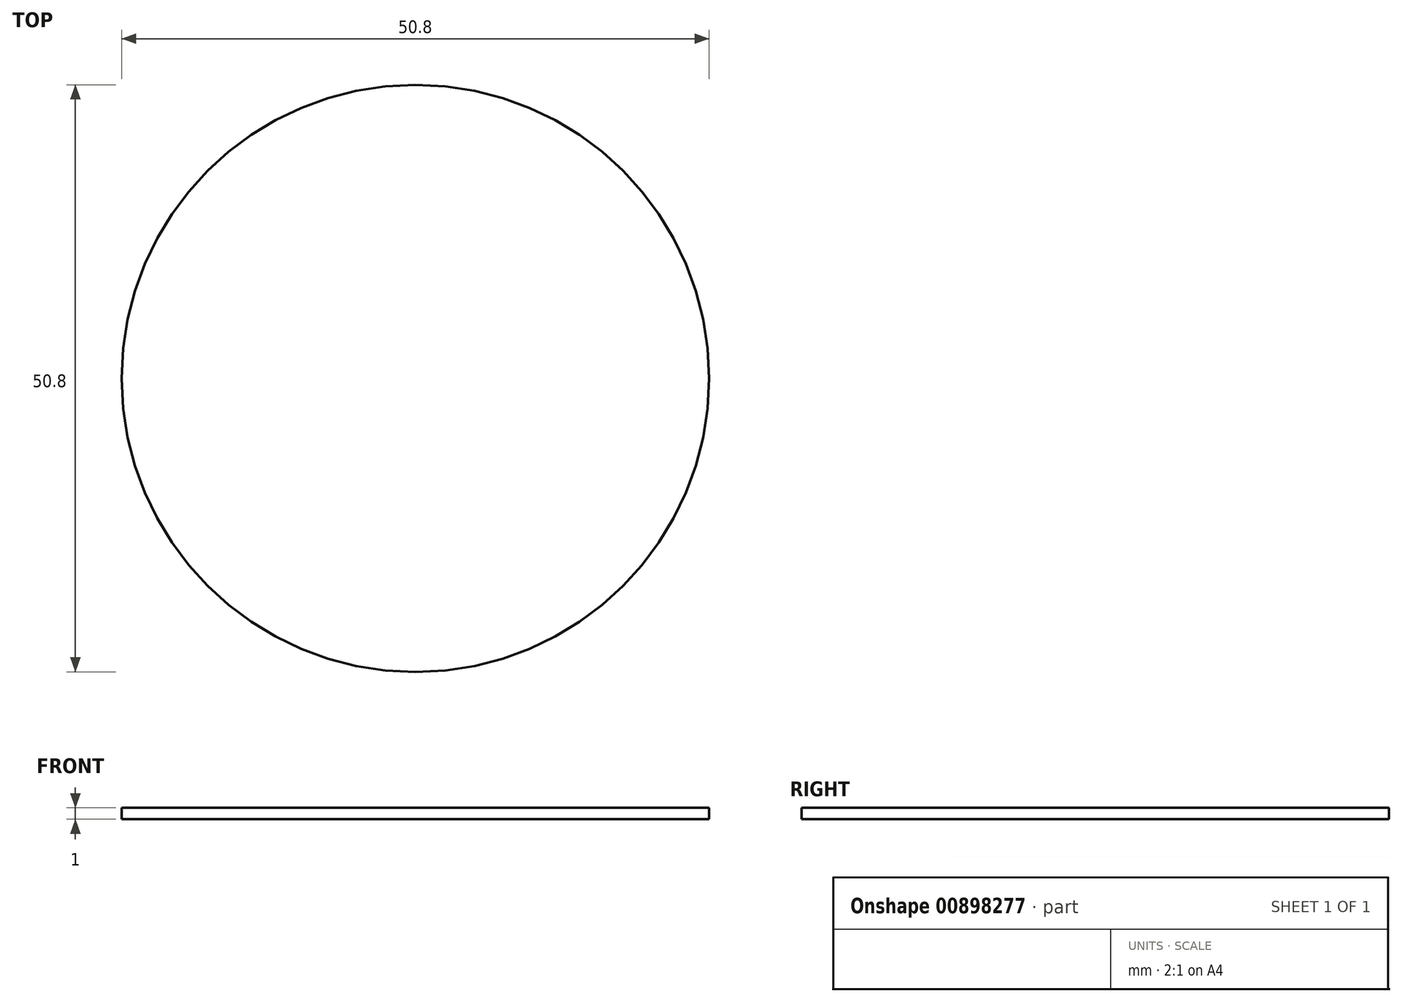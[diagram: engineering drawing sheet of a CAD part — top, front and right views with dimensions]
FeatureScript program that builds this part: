
annotation { "Feature Type Name" : "Feature", "Feature Type Description" : "" }
export const myFeature = defineFeature(function(context is Context, id is Id, definition is map)
    precondition{}
    {
        {
            var Q0;
            Q0=qCreatedBy(makeId("Top.planeOp"),FACE);
            var sketch = newSketch(context, id + "F0", { "sketchPlane" : qUnion([Q0])});
            skCircle(sketch, "E0", {"center": v(0, 0) * mm, "radius": 25.4 * mm});
            skSolve(sketch);
        }
        {
            var Q0;
            Q0=makeQuery(id+"F0.imprint","IMPRINT",FACE,{"disambiguationData":[TD([[makeQuery(id+"F0.imprint","IMPRINT",EDGE,{"derivedFrom":sQuery(id+"F0.wireOp",EDGE,"E0")}),1.0]])]});
            extrude(context, id + "F1", {"entities" : qUnion([Q0]), "depth" : 1 * mm, "offsetDistance" : 25.4 * mm});
        }
    });
